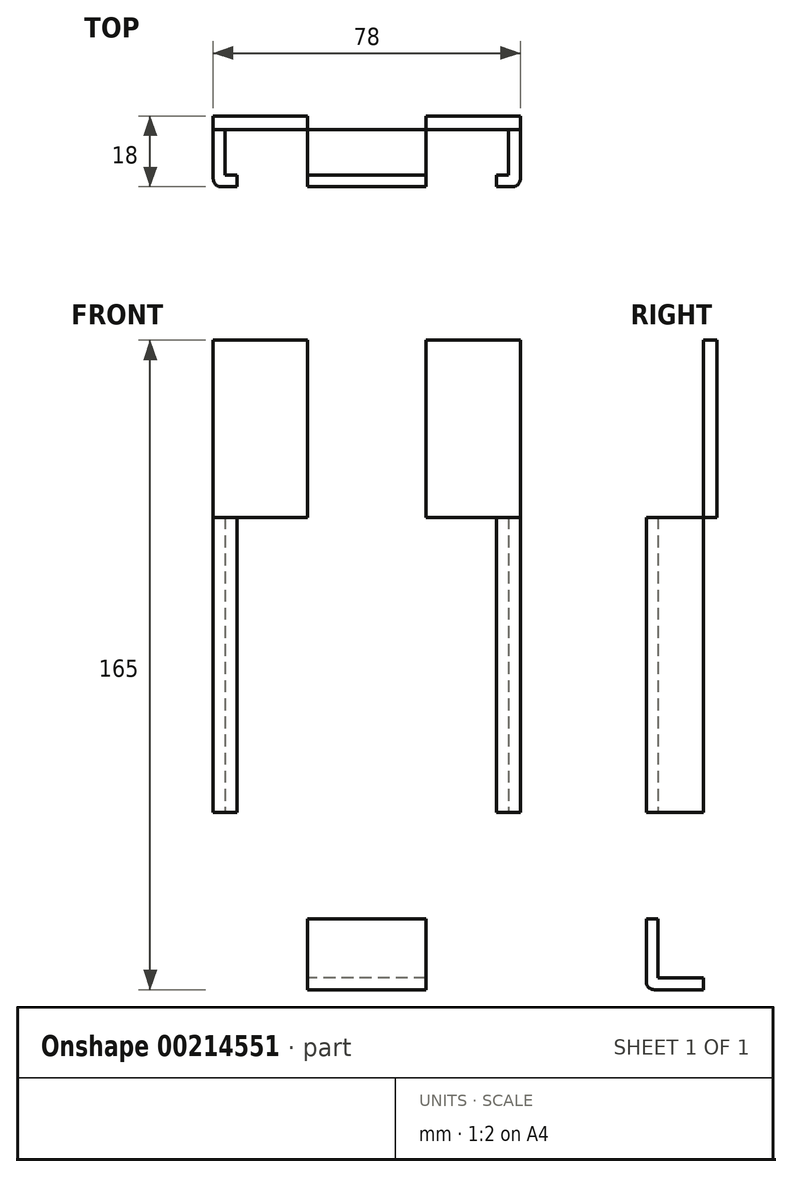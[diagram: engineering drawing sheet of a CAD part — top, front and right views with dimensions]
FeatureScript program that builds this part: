
annotation { "Feature Type Name" : "Feature", "Feature Type Description" : "" }
export const myFeature = defineFeature(function(context is Context, id is Id, definition is map)
    precondition{}
    {
        {
            var Q0;
            Q0=qCreatedBy(makeId("Front.planeOp"),FACE);
            var sketch = newSketch(context, id + "F0", { "sketchPlane" : qUnion([Q0])});
            skLineSegment(sketch, "E0.bottom", {"start": v(-39, 82.5) * mm, "end": v(39, 82.5) * mm});
            skLineSegment(sketch, "E0.top", {"start": v(-39, -82.5) * mm, "end": v(39, -82.5) * mm});
            skLineSegment(sketch, "E0.left", {"start": v(-39, 82.5) * mm, "end": v(-39, -82.5) * mm});
            skLineSegment(sketch, "E0.right", {"start": v(39, 82.5) * mm, "end": v(39, -82.5) * mm});
            skPoint(sketch, "E0.middle", {"position": v(0, 0) * mm});
            skLineSegment(sketch, "E1.bottom", {"start": v(-39, -37.5) * mm, "end": v(-15, -37.5) * mm});
            skLineSegment(sketch, "E1.top", {"start": v(-39, -82.5) * mm, "end": v(-15, -82.5) * mm});
            skLineSegment(sketch, "E1.left", {"start": v(-39, -37.5) * mm, "end": v(-39, -82.5) * mm});
            skLineSegment(sketch, "E1.right", {"start": v(-15, -37.5) * mm, "end": v(-15, -82.5) * mm});
            skLineSegment(sketch, "E2.bottom", {"start": v(39, -82.5) * mm, "end": v(15, -82.5) * mm});
            skLineSegment(sketch, "E2.top", {"start": v(39, -37.5) * mm, "end": v(15, -37.5) * mm});
            skLineSegment(sketch, "E2.left", {"start": v(39, -82.5) * mm, "end": v(39, -37.5) * mm});
            skLineSegment(sketch, "E2.right", {"start": v(15, -82.5) * mm, "end": v(15, -37.5) * mm});
            skLineSegment(sketch, "E3.bottom", {"start": v(-39, 82.5) * mm, "end": v(-15, 82.5) * mm});
            skLineSegment(sketch, "E3.top", {"start": v(-39, 37.5) * mm, "end": v(-15, 37.5) * mm});
            skLineSegment(sketch, "E3.left", {"start": v(-39, 82.5) * mm, "end": v(-39, 37.5) * mm});
            skLineSegment(sketch, "E3.right", {"start": v(-15, 82.5) * mm, "end": v(-15, 37.5) * mm});
            skLineSegment(sketch, "E4.bottom", {"start": v(39, 82.5) * mm, "end": v(15, 82.5) * mm});
            skLineSegment(sketch, "E4.top", {"start": v(39, 37.5) * mm, "end": v(15, 37.5) * mm});
            skLineSegment(sketch, "E4.left", {"start": v(39, 82.5) * mm, "end": v(39, 37.5) * mm});
            skLineSegment(sketch, "E4.right", {"start": v(15, 82.5) * mm, "end": v(15, 37.5) * mm});
            skSolve(sketch);
        }
        {
            var Q0;
            Q0=makeQuery(id+"F0.imprint","IMPRINT",FACE,{"disambiguationData":[TD([[makeQuery(id+"F0.imprint","IMPRINT",EDGE,{"derivedFrom":sQuery(id+"F0.wireOp",EDGE,"E0.bottom")}),-1.0]])]});
            extrude(context, id + "F1", {"entities" : qUnion([Q0]), "depth" : 3.5 * mm});
        }
        {
            var Q0;
            Q0=makeQuery(id+"F1.opExtrude","CAP_FACE",FACE,{"disambiguationData":[OSD([sQuery(id+"F0.wireOp",EDGE,"E0.bottom"),sQuery(id+"F0.wireOp",EDGE,"E0.top"),sQuery(id+"F0.wireOp",EDGE,"E0.left"),sQuery(id+"F0.wireOp",EDGE,"E0.right"),sQuery(id+"F0.wireOp",EDGE,"E1.bottom"),sQuery(id+"F0.wireOp",EDGE,"E1.right"),sQuery(id+"F0.wireOp",EDGE,"E2.top"),sQuery(id+"F0.wireOp",EDGE,"E2.right"),sQuery(id+"F0.wireOp",EDGE,"E3.top"),sQuery(id+"F0.wireOp",EDGE,"E3.right"),sQuery(id+"F0.wireOp",EDGE,"E4.top"),sQuery(id+"F0.wireOp",EDGE,"E4.right")])],"isStart":false});
            var sketch = newSketch(context, id + "F2", { "sketchPlane" : qUnion([Q0])});
            skLineSegment(sketch, "E5.bottom", {"start": v(-15, -82.5) * mm, "end": v(15, -82.5) * mm});
            skLineSegment(sketch, "E5.top", {"start": v(-15, -79.5) * mm, "end": v(15, -79.5) * mm});
            skLineSegment(sketch, "E5.left", {"start": v(-15, -82.5) * mm, "end": v(-15, -79.5) * mm});
            skLineSegment(sketch, "E5.right", {"start": v(15, -82.5) * mm, "end": v(15, -79.5) * mm});
            skSolve(sketch);
        }
        {
            var Q0;
            Q0=makeQuery(id+"F2.imprint","IMPRINT",FACE,{"disambiguationData":[TD([[makeQuery(id+"F2.imprint","IMPRINT",EDGE,{"derivedFrom":sQuery(id+"F2.wireOp",EDGE,"E5.bottom")}),1.0]])]});
            extrude(context, id + "F3", {"entities" : qUnion([Q0]), "operationType" : NewBodyOperationType.ADD, "depth" : 14.5 * mm});
        }
        {
            var Q0;
            Q0=makeQuery(id+"F3.opExtrude","SWEPT_FACE",FACE,{"disambiguationData":[OSD([sQuery(id+"F2.wireOp",EDGE,"E5.top")])]});
            var sketch = newSketch(context, id + "F4", { "sketchPlane" : qUnion([Q0])});
            skLineSegment(sketch, "E6.bottom", {"start": v(15, -18) * mm, "end": v(-15, -18) * mm});
            skLineSegment(sketch, "E6.top", {"start": v(15, -15) * mm, "end": v(-15, -15) * mm});
            skLineSegment(sketch, "E6.left", {"start": v(15, -18) * mm, "end": v(15, -15) * mm});
            skLineSegment(sketch, "E6.right", {"start": v(-15, -18) * mm, "end": v(-15, -15) * mm});
            skSolve(sketch);
        }
        {
            var Q0;
            Q0=makeQuery(id+"F4.imprint","IMPRINT",FACE,{"disambiguationData":[TD([[makeQuery(id+"F4.imprint","IMPRINT",EDGE,{"derivedFrom":sQuery(id+"F4.wireOp",EDGE,"E6.bottom")}),1.0]])]});
            extrude(context, id + "F5", {"entities" : qUnion([Q0]), "operationType" : NewBodyOperationType.ADD, "depth" : 15 * mm});
        }
        {
            var Q0;
            Q0=makeQuery(id+"F1.opExtrude","CAP_FACE",FACE,{"disambiguationData":[OSD([sQuery(id+"F0.wireOp",EDGE,"E0.bottom"),sQuery(id+"F0.wireOp",EDGE,"E0.top"),sQuery(id+"F0.wireOp",EDGE,"E0.left"),sQuery(id+"F0.wireOp",EDGE,"E0.right"),sQuery(id+"F0.wireOp",EDGE,"E1.bottom"),sQuery(id+"F0.wireOp",EDGE,"E1.right"),sQuery(id+"F0.wireOp",EDGE,"E2.top"),sQuery(id+"F0.wireOp",EDGE,"E2.right"),sQuery(id+"F0.wireOp",EDGE,"E3.top"),sQuery(id+"F0.wireOp",EDGE,"E3.right"),sQuery(id+"F0.wireOp",EDGE,"E4.top"),sQuery(id+"F0.wireOp",EDGE,"E4.right")])],"isStart":false});
            var sketch = newSketch(context, id + "F6", { "sketchPlane" : qUnion([Q0])});
            skLineSegment(sketch, "E7.bottom", {"start": v(39, 37.5) * mm, "end": v(36, 37.5) * mm});
            skLineSegment(sketch, "E7.top", {"start": v(39, -37.5) * mm, "end": v(36, -37.5) * mm});
            skLineSegment(sketch, "E7.left", {"start": v(39, 37.5) * mm, "end": v(39, -37.5) * mm});
            skLineSegment(sketch, "E7.right", {"start": v(36, 37.5) * mm, "end": v(36, -37.5) * mm});
            skLineSegment(sketch, "E8.bottom", {"start": v(-39, 37.5) * mm, "end": v(-36, 37.5) * mm});
            skLineSegment(sketch, "E8.top", {"start": v(-39, -37.5) * mm, "end": v(-36, -37.5) * mm});
            skLineSegment(sketch, "E8.left", {"start": v(-39, 37.5) * mm, "end": v(-39, -37.5) * mm});
            skLineSegment(sketch, "E8.right", {"start": v(-36, 37.5) * mm, "end": v(-36, -37.5) * mm});
            skSolve(sketch);
        }
        {
            var Q0;
            Q0=makeQuery(id+"F6.imprint","IMPRINT",FACE,{"disambiguationData":[TD([[makeQuery(id+"F6.imprint","IMPRINT",EDGE,{"derivedFrom":sQuery(id+"F6.wireOp",EDGE,"E8.bottom")}),-1.0]])]});
            extrude(context, id + "F7", {"entities" : qUnion([Q0]), "operationType" : NewBodyOperationType.ADD, "depth" : 14.5 * mm});
        }
        {
            var Q0;
            Q0=makeQuery(id+"F1.opExtrude","CAP_FACE",FACE,{"disambiguationData":[OSD([sQuery(id+"F0.wireOp",EDGE,"E0.bottom"),sQuery(id+"F0.wireOp",EDGE,"E0.top"),sQuery(id+"F0.wireOp",EDGE,"E0.left"),sQuery(id+"F0.wireOp",EDGE,"E0.right"),sQuery(id+"F0.wireOp",EDGE,"E1.bottom"),sQuery(id+"F0.wireOp",EDGE,"E1.right"),sQuery(id+"F0.wireOp",EDGE,"E2.top"),sQuery(id+"F0.wireOp",EDGE,"E2.right"),sQuery(id+"F0.wireOp",EDGE,"E3.top"),sQuery(id+"F0.wireOp",EDGE,"E3.right"),sQuery(id+"F0.wireOp",EDGE,"E4.top"),sQuery(id+"F0.wireOp",EDGE,"E4.right")])],"isStart":false});
            var sketch = newSketch(context, id + "F8", { "sketchPlane" : qUnion([Q0])});
            skLineSegment(sketch, "E9.bottom", {"start": v(39, 37.5) * mm, "end": v(36, 37.5) * mm});
            skLineSegment(sketch, "E9.top", {"start": v(39, -37.5) * mm, "end": v(36, -37.5) * mm});
            skLineSegment(sketch, "E9.left", {"start": v(39, 37.5) * mm, "end": v(39, -37.5) * mm});
            skLineSegment(sketch, "E9.right", {"start": v(36, 37.5) * mm, "end": v(36, -37.5) * mm});
            skSolve(sketch);
        }
        {
            var Q0;
            Q0=makeQuery(id+"F8.imprint","IMPRINT",FACE,{"disambiguationData":[TD([[makeQuery(id+"F8.imprint","IMPRINT",EDGE,{"derivedFrom":sQuery(id+"F8.wireOp",EDGE,"E9.bottom")}),1.0]])]});
            extrude(context, id + "F9", {"entities" : qUnion([Q0]), "operationType" : NewBodyOperationType.ADD, "depth" : 14.5 * mm});
        }
        {
            var Q0;
            Q0=makeQuery(id+"F7.opExtrude","SWEPT_FACE",FACE,{"disambiguationData":[OSD([sQuery(id+"F6.wireOp",EDGE,"E8.right")])]});
            var sketch = newSketch(context, id + "F10", { "sketchPlane" : qUnion([Q0])});
            skLineSegment(sketch, "E10.bottom", {"start": v(-18, 37.5) * mm, "end": v(-15, 37.5) * mm});
            skLineSegment(sketch, "E10.top", {"start": v(-18, -37.5) * mm, "end": v(-15, -37.5) * mm});
            skLineSegment(sketch, "E10.left", {"start": v(-18, 37.5) * mm, "end": v(-18, -37.5) * mm});
            skLineSegment(sketch, "E10.right", {"start": v(-15, 37.5) * mm, "end": v(-15, -37.5) * mm});
            skSolve(sketch);
        }
        {
            var Q0;
            Q0=makeQuery(id+"F10.imprint","IMPRINT",FACE,{"disambiguationData":[TD([[makeQuery(id+"F10.imprint","IMPRINT",EDGE,{"derivedFrom":sQuery(id+"F10.wireOp",EDGE,"E10.bottom")}),-1.0]])]});
            extrude(context, id + "F11", {"entities" : qUnion([Q0]), "operationType" : NewBodyOperationType.ADD, "depth" : 3 * mm});
        }
        {
            var Q0;
            Q0=makeQuery(id+"F9.opExtrude","SWEPT_FACE",FACE,{"disambiguationData":[OSD([sQuery(id+"F8.wireOp",EDGE,"E9.right")])]});
            var sketch = newSketch(context, id + "F12", { "sketchPlane" : qUnion([Q0])});
            skLineSegment(sketch, "E11.bottom", {"start": v(18, 37.5) * mm, "end": v(15, 37.5) * mm});
            skLineSegment(sketch, "E11.top", {"start": v(18, -37.5) * mm, "end": v(15, -37.5) * mm});
            skLineSegment(sketch, "E11.left", {"start": v(18, 37.5) * mm, "end": v(18, -37.5) * mm});
            skLineSegment(sketch, "E11.right", {"start": v(15, 37.5) * mm, "end": v(15, -37.5) * mm});
            skSolve(sketch);
        }
        {
            var Q0;
            Q0=makeQuery(id+"F12.imprint","IMPRINT",FACE,{"disambiguationData":[TD([[makeQuery(id+"F12.imprint","IMPRINT",EDGE,{"derivedFrom":sQuery(id+"F12.wireOp",EDGE,"E11.bottom")}),1.0]])]});
            extrude(context, id + "F13", {"entities" : qUnion([Q0]), "operationType" : NewBodyOperationType.ADD, "depth" : 3 * mm});
        }
        {
            var Q0;
            Q0=makeQuery(id+"F9.opExtrude","CAP_EDGE",EDGE,{"disambiguationData":[OSD([sQuery(id+"F8.wireOp",EDGE,"E9.left")])],"isStart":false});
            fillet(context, id + "F14", {"entities" : qUnion([Q0]), "radius" : 2 * mm, "tangentPropagation" : true, "allowEdgeOverflow" : false});
        }
        {
            var Q0;
            Q0=makeQuery(id+"F7.opExtrude","CAP_EDGE",EDGE,{"disambiguationData":[OSD([sQuery(id+"F6.wireOp",EDGE,"E8.left")])],"isStart":false});
            fillet(context, id + "F15", {"entities" : qUnion([Q0]), "radius" : 2 * mm, "tangentPropagation" : true, "allowEdgeOverflow" : false});
        }
        {
            var Q0;
            Q0=makeQuery(id+"F3.opExtrude","CAP_EDGE",EDGE,{"disambiguationData":[OSD([sQuery(id+"F2.wireOp",EDGE,"E5.bottom")])],"isStart":false});
            fillet(context, id + "F16", {"entities" : qUnion([Q0]), "radius" : 2 * mm, "tangentPropagation" : true, "allowEdgeOverflow" : false});
        }
        {
            var Q0;
            Q0=makeQuery(id+"F1.opExtrude","CAP_FACE",FACE,{"disambiguationData":[OSD([sQuery(id+"F0.wireOp",EDGE,"E0.bottom"),sQuery(id+"F0.wireOp",EDGE,"E0.top"),sQuery(id+"F0.wireOp",EDGE,"E0.left"),sQuery(id+"F0.wireOp",EDGE,"E0.right"),sQuery(id+"F0.wireOp",EDGE,"E1.bottom"),sQuery(id+"F0.wireOp",EDGE,"E1.right"),sQuery(id+"F0.wireOp",EDGE,"E2.top"),sQuery(id+"F0.wireOp",EDGE,"E2.right"),sQuery(id+"F0.wireOp",EDGE,"E3.top"),sQuery(id+"F0.wireOp",EDGE,"E3.right"),sQuery(id+"F0.wireOp",EDGE,"E4.top"),sQuery(id+"F0.wireOp",EDGE,"E4.right")])],"isStart":false});
            var sketch = newSketch(context, id + "F17", { "sketchPlane" : qUnion([Q0])});
            skCircle(sketch, "E12", {"center": v(0, 74.8) * mm, "radius": 1.87 * mm});
            skSolve(sketch);
        }
        {
            var Q0;
            Q0=sQuery(id+"F17.wireOp",VERTEX,"E12.center");
            var Q1;
            Q1=makeQuery(id+"F1.opExtrude","SWEPT_BODY",BODY,{"disambiguationData":[OSD([sQuery(id+"F0.wireOp",EDGE,"E0.bottom"),sQuery(id+"F0.wireOp",EDGE,"E0.top"),sQuery(id+"F0.wireOp",EDGE,"E0.left"),sQuery(id+"F0.wireOp",EDGE,"E0.right"),sQuery(id+"F0.wireOp",EDGE,"E1.bottom"),sQuery(id+"F0.wireOp",EDGE,"E1.right"),sQuery(id+"F0.wireOp",EDGE,"E2.top"),sQuery(id+"F0.wireOp",EDGE,"E2.right"),sQuery(id+"F0.wireOp",EDGE,"E3.top"),sQuery(id+"F0.wireOp",EDGE,"E3.right"),sQuery(id+"F0.wireOp",EDGE,"E4.top"),sQuery(id+"F0.wireOp",EDGE,"E4.right")])]});
            hole(context, id + "F18", {"style" : HoleStyle.SIMPLE, "endStyle" : HoleEndStyle.THROUGH, "holeDiameter" : 4.4 * mm, "locations" : qUnion([Q0]), "scope" : qUnion([Q1]), "isTappedThrough" : true});
        }
    });
